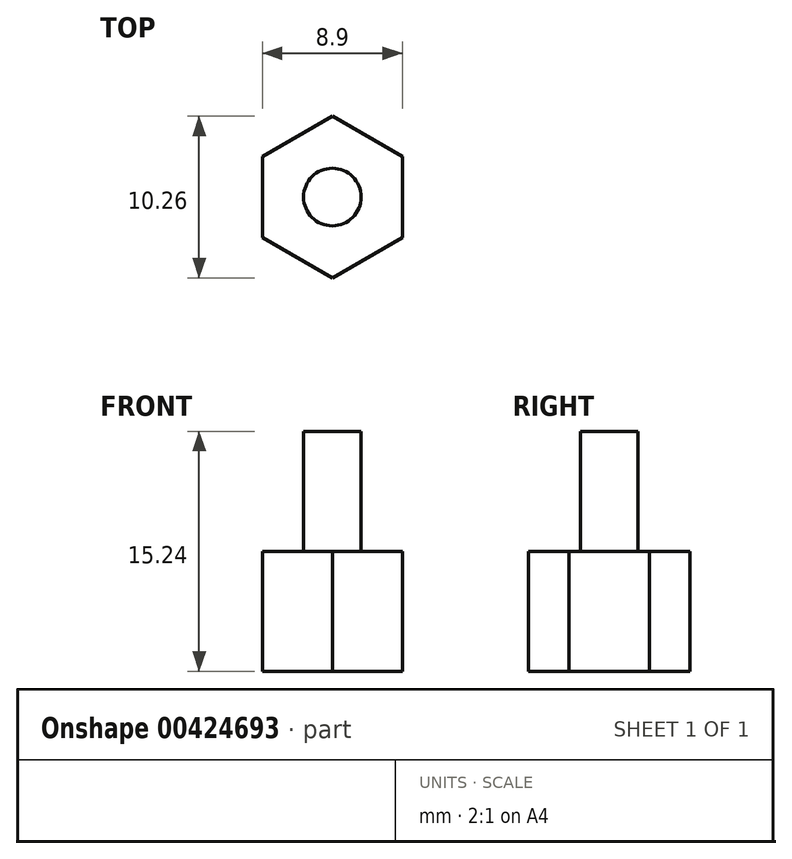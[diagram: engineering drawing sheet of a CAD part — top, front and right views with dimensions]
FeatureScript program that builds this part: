
annotation { "Feature Type Name" : "Feature", "Feature Type Description" : "" }
export const myFeature = defineFeature(function(context is Context, id is Id, definition is map)
    precondition{}
    {
        {
            var Q0;
            Q0=qCreatedBy(makeId("Top.planeOp"),FACE);
            var sketch = newSketch(context, id + "F0", { "sketchPlane" : qUnion([Q0])});
            skCircle(sketch, "E0.cCircle", {"center": v(0, 0) * mm, "radius": 4.45 * mm, "construction": true});
            skLineSegment(sketch, "E0.0", {"start": v(4.45, 2.57) * mm, "end": v(4.45, -2.57) * mm});
            skLineSegment(sketch, "E0.1", {"start": v(4.45, -2.57) * mm, "end": v(0, -5.13) * mm});
            skLineSegment(sketch, "E0.2", {"start": v(0, -5.13) * mm, "end": v(-4.44, -2.57) * mm});
            skLineSegment(sketch, "E0.3", {"start": v(-4.44, -2.57) * mm, "end": v(-4.45, 2.57) * mm});
            skLineSegment(sketch, "E0.4", {"start": v(-4.45, 2.57) * mm, "end": v(0, 5.13) * mm});
            skLineSegment(sketch, "E0.5", {"start": v(0, 5.13) * mm, "end": v(4.45, 2.57) * mm});
            skPoint(sketch, "E0.0.midPoint", {"position": v(4.45, 0) * mm});
            skCircle(sketch, "E1", {"center": v(0, 0) * mm, "radius": 1.83 * mm});
            skSolve(sketch);
        }
        {
            var Q0;
            Q0=makeQuery(id+"F0.imprint","IMPRINT",FACE,{"disambiguationData":[TD([[makeQuery(id+"F0.imprint","IMPRINT",EDGE,{"derivedFrom":sQuery(id+"F0.wireOp",EDGE,"E0.0")}),-1.0]])]});
            extrude(context, id + "F1", {"entities" : qUnion([Q0]), "depth" : 7.62 * mm});
        }
        {
            var Q0;
            Q0=makeQuery(id+"F0.imprint","IMPRINT",FACE,{"disambiguationData":[TD([[makeQuery(id+"F0.imprint","IMPRINT",EDGE,{"derivedFrom":sQuery(id+"F0.wireOp",EDGE,"E1")}),1.0]])]});
            extrude(context, id + "F2", {"entities" : qUnion([Q0]), "operationType" : NewBodyOperationType.ADD, "depth" : 15.24 * mm});
        }
    });
